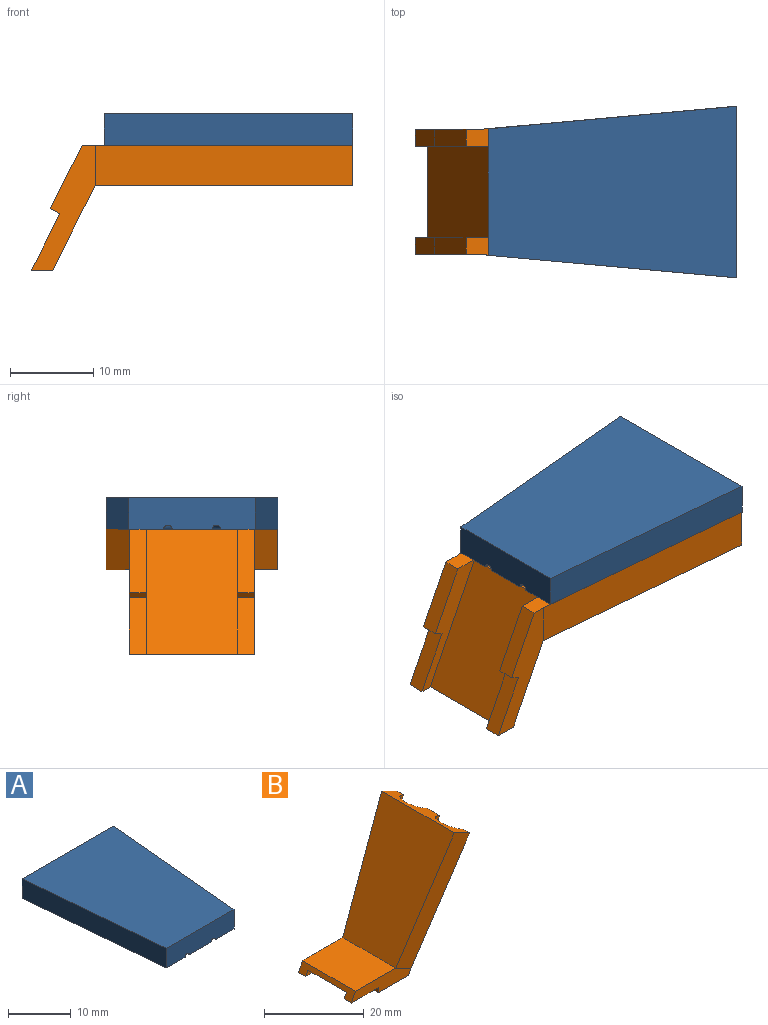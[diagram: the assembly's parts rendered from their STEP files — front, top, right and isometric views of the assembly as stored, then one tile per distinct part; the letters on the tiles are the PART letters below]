
ASSEMBLY  parts=2 mates=1
PART A: 14 faces, bbox 20.6x29.9x3.8 mm
  f0: plane 29.82x6.86mm, normal (0,0,-1), area 82.5mm2, adj f4,f5,f6,f9,f10,f12
  f1: plane 29.82x9.14mm, normal (0,0,-1), area 164.3mm2, adj f3,f4,f6,f9,f10,f11,f12,f13
  f2: plane 29.82x6.86mm, normal (0,0,-1), area 82.5mm2, adj f3,f4,f6,f7,f11,f13
  f3: plane 6.6x3.3mm, normal (0,1,0), area 16.7mm2, adj f1,f2,f11,f13
  f4: plane 20.57x3.81mm, normal (0,1,0), area 44.1mm2, adj f0,f1,f2,f5,f7,f8,f9,f11
  f5: plane 29.82x3.81mm, normal (-1,-0.09,0), area 114.1mm2, adj f0,f4,f6,f8
  f6: plane 15.17x3.81mm, normal (0,-1,0), area 57mm2, adj f0,f1,f2,f5,f7,f8,f12,f13
  f7: plane 29.82x3.81mm, normal (1,-0.09,0), area 114.1mm2, adj f2,f4,f6,f8
  f8: plane 29.82x20.57mm, normal (0,0,1), area 533mm2, adj f4,f5,f6,f7
  f9: cylinder r=3.3mm len=12.78mm, axis (0,1,0), area 132.5mm2, adj f0,f1,f4,f10
  f10: plane 6.6x3.3mm, normal (0,1,0), area 16.7mm2, adj f0,f1,f9,f12
  f11: cylinder r=3.3mm len=12.78mm, axis (0,1,0), area 132.5mm2, adj f1,f2,f3,f4
  f12: cylinder r=0.51mm len=17.3mm, axis (-0.13,0.99,0), area 27.4mm2, adj f0,f1,f6,f10
  f13: cylinder r=0.51mm len=17.3mm, axis (0.13,0.99,0), area 27.4mm2, adj f1,f2,f3,f6
PART B: 22 faces, bbox 30.6x20.6x31.2 mm
  f0: plane 8.51x2.03mm, normal (0,0,-1), area 17.3mm2, adj f2,f5,f14,f20
  f1: plane 2.03x1.27mm, normal (-1,0,0), area 2.6mm2, adj f7,f8,f13,f19
  f2: plane 29x20.57mm, normal (0.89,0,-0.45), area 372.4mm2, adj f0,f4,f5,f7,f8,f11,f12,f15
  f3: plane 7.62x2.03mm, normal (0,0,-1), area 15.5mm2, adj f5,f6,f14,f20
  f4: plane 20.57x4.32mm, normal (0.45,0,0.89), area 65mm2, adj f2,f9,f11,f12,f15,f17
  f5: plane 16.83x3.56mm, normal (0,-1,0), area 43.7mm2, adj f0,f2,f3,f6,f10,f11,f14
  f6: plane 14.99x2.29mm, normal (-0.89,0,0.45), area 22.8mm2, adj f3,f5,f8,f10,f13,f19,f20,f21
  f7: plane 8.51x2.03mm, normal (0,0,-1), area 17.3mm2, adj f1,f2,f8,f19
  f8: plane 16.83x3.56mm, normal (0,1,0), area 43.7mm2, adj f1,f2,f6,f7,f10,f12,f13
  f9: plane 27.6x20.57mm, normal (-0.89,0,0.45), area 548.7mm2, adj f4,f10,f11,f12
  f10: plane 14.99x11.37mm, normal (0,0,1), area 170.4mm2, adj f5,f6,f8,f9
  f11: plane 29.76x18.11mm, normal (-0.04,-1,-0.08), area 149.5mm2, adj f2,f4,f5,f9
  f12: plane 29.76x18.11mm, normal (-0.04,1,-0.08), area 149.5mm2, adj f2,f4,f8,f9
  f13: plane 7.62x2.03mm, normal (0,0,-1), area 15.5mm2, adj f1,f6,f8,f19
  f14: plane 2.03x1.27mm, normal (-1,0,0), area 2.6mm2, adj f0,f3,f5,f20
  f15: cylinder r=3.3mm len=12.9mm, axis (0.45,0,0.89), area 132.5mm2, adj f2,f4,f16
  f16: plane 6.6x2.95mm, normal (0.45,0,0.89), area 17.1mm2, adj f2,f15
  f17: cylinder r=3.3mm len=12.9mm, axis (0.45,0,0.89), area 132.5mm2, adj f2,f4,f18
  f18: plane 6.6x2.95mm, normal (0.45,0,0.89), area 17.1mm2, adj f2,f17
  f19: plane 17.4x2.54mm, normal (0,-1,0), area 32.5mm2, adj f1,f2,f6,f7,f13,f21
  f20: plane 17.4x2.54mm, normal (0,1,0), area 32.5mm2, adj f0,f2,f3,f6,f14,f21
  f21: plane 16.76x10.92mm, normal (0,0,-1), area 183.1mm2, adj f2,f6,f19,f20
PLACE A rot(axis=(0,0,-1),90deg) t=(72.62,-42.24,1.13)mm
PLACE B rot(axis=(0.85,0,0.53),180deg) t=(47.01,-47.03,-14.32)mm
MATE planar B.f2 <-> A.f1  axis (0,0,1) through (57.57,-39.53,1.13)mm
